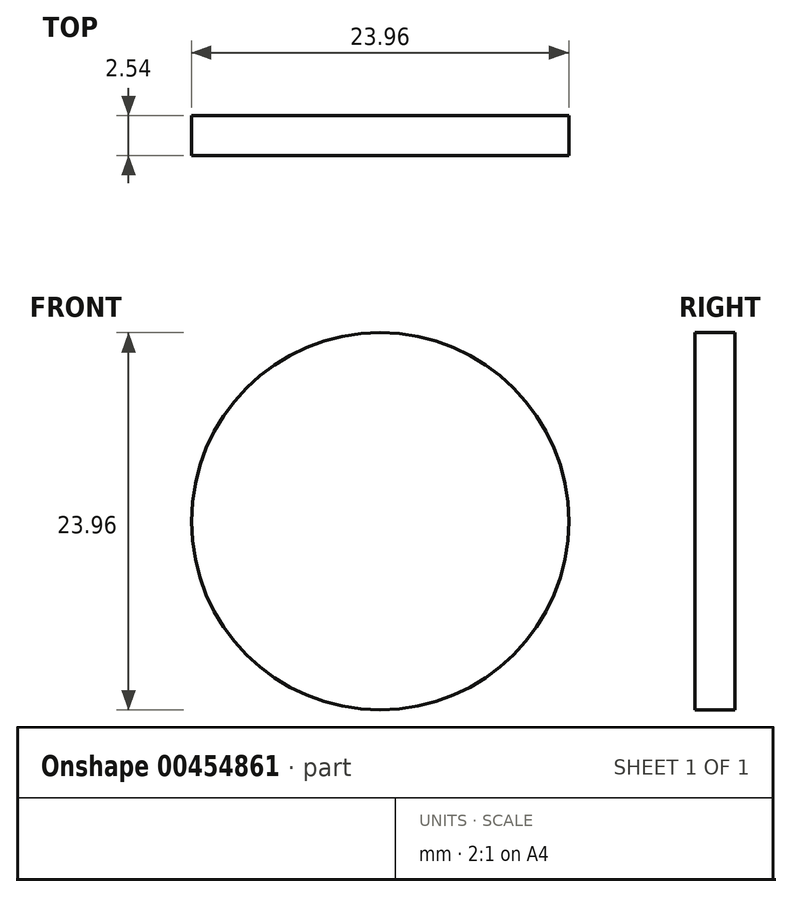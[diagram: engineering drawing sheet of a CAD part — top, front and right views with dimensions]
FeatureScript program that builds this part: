
annotation { "Feature Type Name" : "Feature", "Feature Type Description" : "" }
export const myFeature = defineFeature(function(context is Context, id is Id, definition is map)
    precondition{}
    {
        {
            var Q0;
            Q0=qCreatedBy(makeId("Front.planeOp"),FACE);
            var sketch = newSketch(context, id + "F0", { "sketchPlane" : qUnion([Q0])});
            skCircle(sketch, "E0", {"center": v(0, 0) * mm, "radius": 11.98 * mm});
            skSolve(sketch);
        }
        {
            var Q0;
            Q0 = qSketchRegion(id + "F0", true);
            extrude(context, id + "F1", {"entities" : qUnion([Q0]), "depth" : 2.54 * mm, "offsetDistance" : 25.4 * mm});
        }
    });
